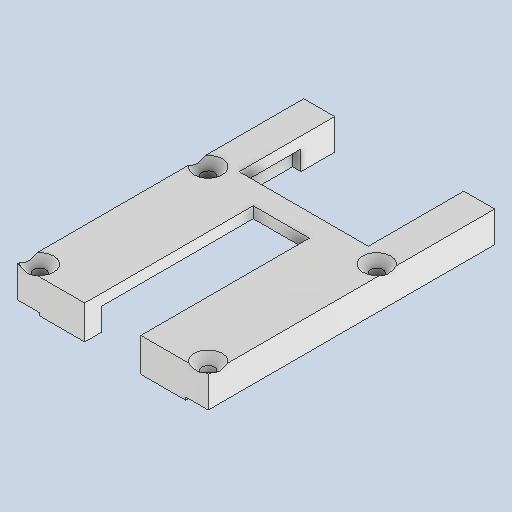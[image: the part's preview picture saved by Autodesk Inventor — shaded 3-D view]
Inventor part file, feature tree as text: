
AUTODESK INVENTOR PART (.ipt)
format: ipt  version: 2025 (Build 290162010, 162A)  size: 202,752 bytes
history: native  units: mm
features: extrude x4, sketch x4, hole x1
ambient origin geometry x8: Origin, YZ Plane, XZ Plane, XY Plane, X Axis, Y Axis, Z Axis, Center Point
bodies: Volumenkörper1 (feature_tree)
feature tree (9):
  extrude  "Extrusion1"  Depth=51.0mm
  extrude  "Extrusion2"  Depth=4.0mm
  hole  "Bohrung1"  [1 undecoded]
  sketch  "Skizze6"  dims[d8=2.2mm d9=6.0mm d10=5.0mm d11=2.0mm d12=90.0deg d13=8.0mm d14=20.594885mm d24=2.0mm d37=19.0mm d38=23.0mm d39=17.0mm d44=4.0mm d47=26.0mm d48=6.0mm d49=2.0mm d50=0.0mm d52=4.0mm d53=0.0mm d54=10.0mm d25=0.5mm d26=0.872665mm d27=0.5mm d28=0.872665mm]
  extrude  "Extrusion5"  Depth=0.5mm
  extrude  "Extrusion6"  Depth=0.5mm
  sketch  "Skizze1"  dims[d0=4.0mm d1=51.0mm]
  sketch  "Skizze2"  dims[d2=26.0mm d3=4.0mm]
  sketch  "Skizze3"  dims[d4=3.5mm d5=0.0mm d6=2.0mm d7=0.0mm]
note: 1 required parameter value undecoded (feature->parameter linkage not recoverable at this tier; creation-order binding heuristic only, values carry confidence <= 0.55)
